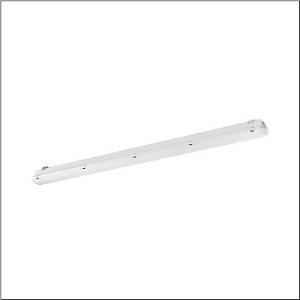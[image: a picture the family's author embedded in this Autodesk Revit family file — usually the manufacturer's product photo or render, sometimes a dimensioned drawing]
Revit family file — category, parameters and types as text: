
# Revit family: monsun_r__11xtreme_mo_51fe10dp460m_82e5
name_source: partatom
category: Lighting Fixtures
units: mm (PartAtom-declared; Revit-internal decimal feet)

## family parameters
Cut with Voids When Loaded = No
Host = Face
Light Source = No
Part Type = Normal
Room Calculation Point = No
Round Connector Dimension = Use Diameter
Shared = No

## types (1)
- --- (1 x LED, 6370 lm, 34.5 W, 4000K)
    Apparent Load = 35 VA
    CIE Flux Codes = 47 77 93 94 100
    Color Rendering = 80
    Color Temperature = 4000K
    Default Elevation = 1800 mm
    Description = Monsun® 11Xtreme MO, damp-proof luminaire, chain hanger, primary optical cover: enclosure, of PMMA, light emission: direct distribution, primary light characteristic: symmetric, installation type: suspended mounting, surface-mounted, horizontal mounting, vertical mounting, LED, rated luminous flux: 6.370lm, luminous efficacy: 185lm/W, light colour: 840, colour temperature: 4000K, control gear: DALI 2, with terminal, 5-pole, max. 2.5mm², mains connection: 220..240V, AC, 50/60Hz, rated input power: 35W, luminaire housing, of glass-fibre reinforced polyester, uncoated, bright grey, incl. chain hanger, length: 1.590mm, width: 90mm, height: 88mm, clip for enclosure, of stainless steel (V2A), ceiling mounting element, of stainless steel (V2A), chain hanger, of stainless steel (V2A), protection rating (complete): IP66, insulation class (complete): insulation class I (protective earthing), certification: CE, ENEC, VDE, UKCA, protection symbol: D, impact resistance: IK04, permissible operating ambient temperature: -35..+55°C, standard: EN 50419, EN 60598-2-1, contact your sales advisor before using the luminaires in applications with unclear chemical exposure, large temperature fluctuations or condensation-forming humidity, LABS conformity tested according to VDMA 24364:2018-05, no direct snow, no direct sun, no direct rain, for indoor or canopied outdoor use, corresponds to IFS (International Featured Standards) requirements for safety and quality in the food industry, packaging unit: 1 piece
    Height = 88 mm
    Lamp = 1 x LED
    Lamp Light Flux = 6370 lm
    Lamp Power = 34.5 W
    Lamp count = 1
    Length = 1590 mm
    Luminous efficacy = 185 lm/W
    Manufacturer = Siteco
    ModVariant = No
    Model = 51FE10DP460M
    Mounting Place = Ceiling
    Mounting Type = Surface mounted
    Number of Poles = 1
    OnlyDefault = Yes
    Power Factor = 1
    Product Name = Monsun® 11Xtreme MO
    Product group = damp-proof luminaire
    ProductGroupID = 300
    Protection Class = Protection class I
    Protection Degree = IP 66
    RLX_Detail_Level = 1
    RLX_Emergency_Light_Flux = 0 lm
    RLX_Emergency_Type = 0
    RLX_Emergency_Type_DB = No
    RlxData = <blob elided: 87197 chars, md5=dd97637c>
    Socket = socket
    Standby Power = 0 W
    System Light Flux = 6370 lm
    System Power = 35 W
    Type Comments = factory setting: luminous flux: 100 % | dim-lin: 254 | 231 mA
    Type Image = l_1349234.jpg
    URL = http://relux.com
    VarID = @adj_017670
    Voltage = 0 V
    Weight = 0.00 kg
    Width = 90 mm

## geometry (parser evidence)
native form markers: Blend x4, Sweep x11
no freeform markers — native parametric forms only
